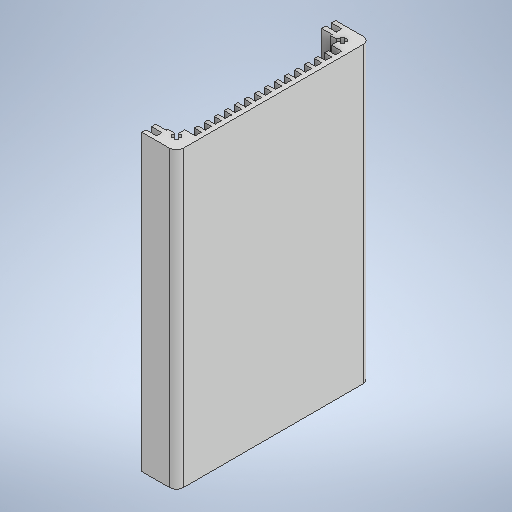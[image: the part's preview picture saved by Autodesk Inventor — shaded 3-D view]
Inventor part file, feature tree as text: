
AUTODESK INVENTOR PART (.ipt)
format: ipt  version: 2025 (Build 290162000, 162)  size: 416,768 bytes
history: native  units: in
note: dims shown in document units (in); Inventor stores cm internally (conversion verified against a paired STEP export)
features: sketch x2, extrude x1, fillet x1
ambient origin geometry x8: Origin, YZ Plane, XZ Plane, XY Plane, X Axis, Y Axis, Z Axis, Center Point
bodies: Solid1 (feature_tree)
feature tree (4):
  extrude  "Extrusion1"  Depth=0.3937in
  fillet  "Fillet1"  Radius=1.1024in
  sketch  "Sketch1"  dims[d0=2.2047in d1=0.3937in d3=1.1024in]
  sketch  "Sketch Rectangular Pattern1"  dims[d4=0.0472in d5=0.1181in d6=0.063in d7=0.0472in d9=0.9449in d10=0.1575in d11=0.0394in d12=45.0deg d13=0.0394in d14=0.0394in d15=0.0197in d16=0.0197in d17=0.0197in d18=0.0197in d20=0.0197in d21=0.0197in d25=0.0354in d26=0.0551in d27=0.0827in d28=0.0433in d29=0.0354in d30=2.7559in d32=0.1142in d33=0.3937in d35=0.3937in d37=0.0354in d38=0.1181in d39=3.3465in d40=0.0in d41=0.0787in]
